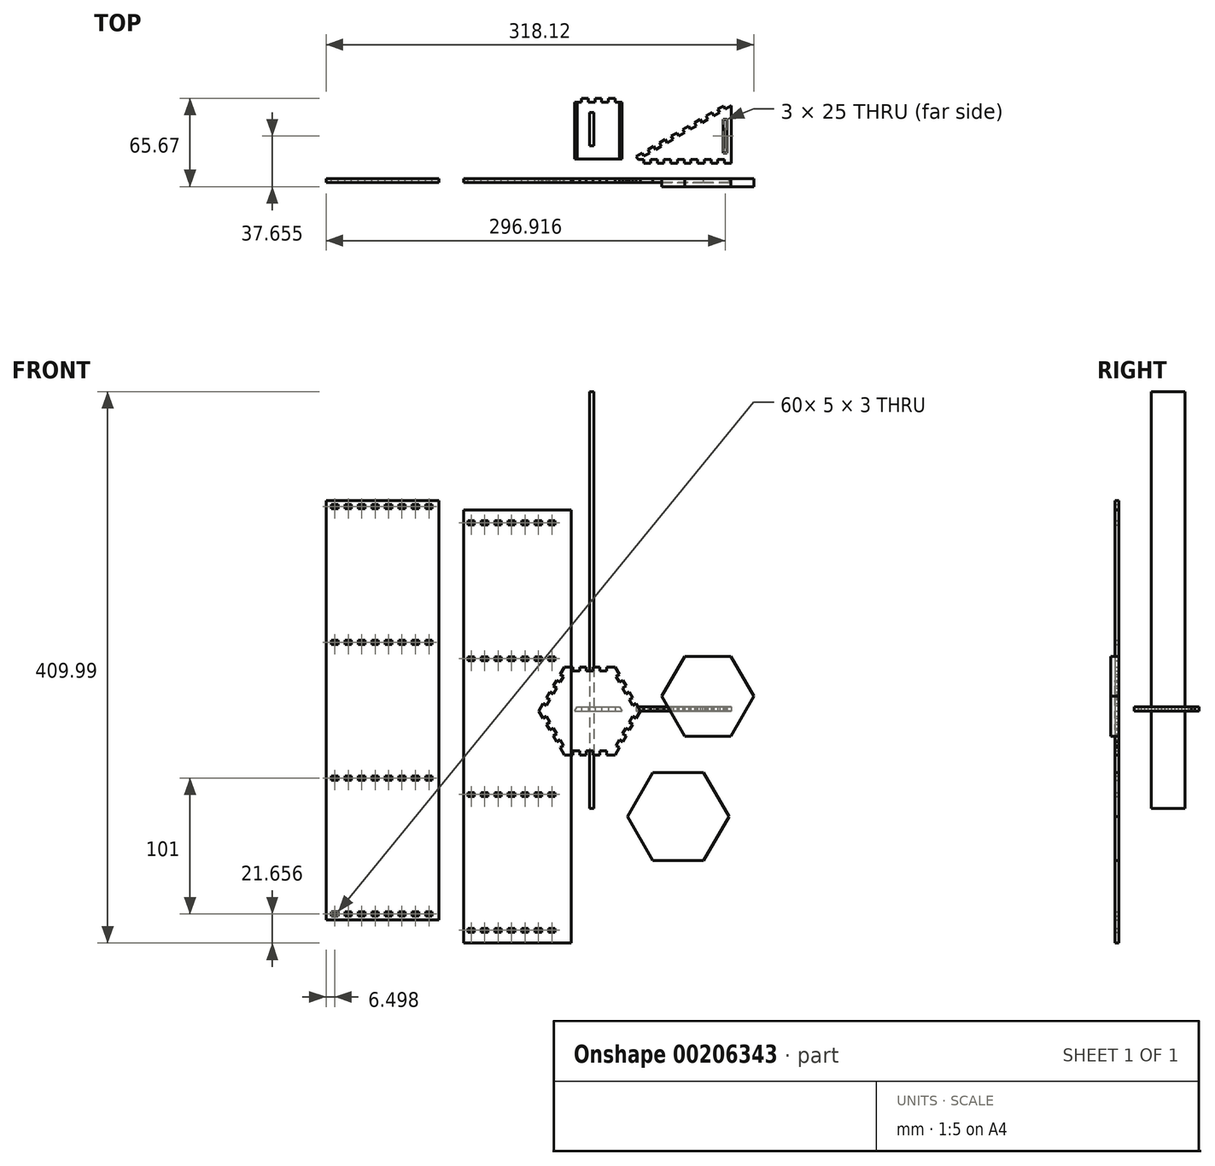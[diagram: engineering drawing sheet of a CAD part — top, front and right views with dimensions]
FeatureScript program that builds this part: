
annotation { "Feature Type Name" : "Feature", "Feature Type Description" : "" }
export const myFeature = defineFeature(function(context is Context, id is Id, definition is map)
    precondition{}
    {
        {
            var Q0;
            Q0=qCreatedBy(makeId("Top.planeOp"),FACE);
            var sketch = newSketch(context, id + "F0", { "sketchPlane" : qUnion([Q0])});
            skLineSegment(sketch, "E0.top", {"start": v(-11.06, 14.67) * mm, "end": v(23.94, 14.67) * mm});
            skLineSegment(sketch, "E0.left", {"start": v(-11.06, 56.67) * mm, "end": v(-11.06, 14.67) * mm});
            skLineSegment(sketch, "E0.right", {"start": v(23.94, 56.67) * mm, "end": v(23.94, 14.67) * mm});
            skLineSegment(sketch, "E1", {"start": v(-6.06, 56.67) * mm, "end": v(-6.06, 59.67) * mm});
            skLineSegment(sketch, "E2", {"start": v(-6.06, 59.67) * mm, "end": v(-1.06, 59.67) * mm});
            skLineSegment(sketch, "E3", {"start": v(-1.06, 59.67) * mm, "end": v(-1.06, 56.67) * mm});
            skLineSegment(sketch, "E4", {"start": v(-11.06, 56.67) * mm, "end": v(-6.06, 56.67) * mm});
            skLineSegment(sketch, "E5", {"start": v(-1.06, 56.67) * mm, "end": v(3.94, 56.67) * mm});
            skLineSegment(sketch, "E6", {"start": v(3.94, 56.67) * mm, "end": v(3.94, 59.67) * mm});
            skLineSegment(sketch, "E7", {"start": v(3.94, 59.67) * mm, "end": v(8.94, 59.67) * mm});
            skLineSegment(sketch, "E8", {"start": v(8.94, 59.67) * mm, "end": v(8.94, 56.67) * mm});
            skLineSegment(sketch, "E9", {"start": v(8.94, 56.67) * mm, "end": v(13.94, 56.67) * mm});
            skLineSegment(sketch, "E10", {"start": v(13.94, 56.67) * mm, "end": v(13.94, 59.67) * mm});
            skLineSegment(sketch, "E11", {"start": v(13.94, 59.67) * mm, "end": v(18.94, 59.67) * mm});
            skLineSegment(sketch, "E12", {"start": v(18.94, 59.67) * mm, "end": v(18.94, 56.67) * mm});
            skLineSegment(sketch, "E13", {"start": v(18.94, 56.67) * mm, "end": v(23.94, 56.67) * mm});
            skSolve(sketch);
        }
        {
            var Q0;
            Q0 = qSketchRegion(id + "F0", true);
            extrude(context, id + "F1", {"entities" : qUnion([Q0]), "depth" : 3 * mm});
        }
        {
            var Q0;
            Q0=makeQuery(id+"F1.opExtrude","CAP_EDGE",EDGE,{"disambiguationData":[OSD([sQuery(id+"F0.wireOp",EDGE,"E0.left")])],"isStart":false});
            var Q1;
            Q1=makeQuery(id+"F1.opExtrude","CAP_EDGE",EDGE,{"disambiguationData":[OSD([sQuery(id+"F0.wireOp",EDGE,"E0.right")])],"isStart":false});
            chamfer(context, id + "F2", {"entities" : qUnion([Q0, Q1]), "chamferType" : ChamferType.OFFSET_ANGLE, "width" : 1.73 * mm, "oppositeDirection" : false, "angle" : 60 * degree, "tangentPropagation" : true});
        }
        {
            var Q0;
            Q0=qCreatedBy(makeId("Front.planeOp"),FACE);
            var sketch = newSketch(context, id + "F3", { "sketchPlane" : qUnion([Q0])});
            skCircle(sketch, "E14.cCircle", {"center": v(0, 0) * mm, "radius": 32.74 * mm, "construction": true});
            skLineSegment(sketch, "E14.0", {"start": v(37.8, 0) * mm, "end": v(34.6, -5.54) * mm});
            skLineSegment(sketch, "E14.1", {"start": v(18.9, -32.74) * mm, "end": v(12.5, -32.74) * mm});
            skLineSegment(sketch, "E14.2", {"start": v(-18.9, -32.74) * mm, "end": v(-22.1, -27.2) * mm});
            skLineSegment(sketch, "E14.3", {"start": v(-37.8, 0) * mm, "end": v(-34.6, 5.54) * mm});
            skLineSegment(sketch, "E14.4", {"start": v(-18.9, 32.74) * mm, "end": v(-12.5, 32.74) * mm});
            skLineSegment(sketch, "E14.5", {"start": v(18.9, 32.74) * mm, "end": v(22.1, 27.2) * mm});
            skPoint(sketch, "E14.0.midPoint", {"position": v(28.35, -16.37) * mm});
            skLineSegment(sketch, "E15", {"start": v(-12.5, 32.74) * mm, "end": v(-12.5, 29.74) * mm});
            skLineSegment(sketch, "E16", {"start": v(-12.5, 29.74) * mm, "end": v(-7.5, 29.74) * mm});
            skLineSegment(sketch, "E17", {"start": v(-7.5, 29.74) * mm, "end": v(-7.5, 32.74) * mm});
            skLineSegment(sketch, "E18", {"start": v(12.5, 32.74) * mm, "end": v(12.5, 29.74) * mm});
            skLineSegment(sketch, "E19", {"start": v(12.5, 29.74) * mm, "end": v(7.5, 29.74) * mm});
            skLineSegment(sketch, "E20", {"start": v(7.5, 29.74) * mm, "end": v(7.5, 32.74) * mm});
            skLineSegment(sketch, "E21", {"start": v(7.5, 32.74) * mm, "end": v(2.5, 32.74) * mm});
            skLineSegment(sketch, "E22", {"start": v(-2.5, 32.74) * mm, "end": v(-2.5, 29.74) * mm});
            skLineSegment(sketch, "E23", {"start": v(-2.5, 29.74) * mm, "end": v(2.5, 29.74) * mm});
            skLineSegment(sketch, "E24", {"start": v(2.5, 29.74) * mm, "end": v(2.5, 32.74) * mm});
            skLineSegment(sketch, "E25.trimOffspring", {"start": v(2.5, 32.74) * mm, "end": v(7.5, 32.74) * mm});
            skLineSegment(sketch, "E26.trimOffspring", {"start": v(-7.5, 32.74) * mm, "end": v(-2.5, 32.74) * mm});
            skLineSegment(sketch, "E27.trimOffspring", {"start": v(12.5, 32.74) * mm, "end": v(18.9, 32.74) * mm});
            skLineSegment(sketch, "E28", {"start": v(-34.6, 5.54) * mm, "end": v(-32, 4.04) * mm});
            skLineSegment(sketch, "E29", {"start": v(-32, 4.04) * mm, "end": v(-29.5, 8.37) * mm});
            skLineSegment(sketch, "E30", {"start": v(-29.5, 8.37) * mm, "end": v(-32.1, 9.87) * mm});
            skLineSegment(sketch, "E31", {"start": v(-29.6, 14.2) * mm, "end": v(-27, 12.7) * mm});
            skLineSegment(sketch, "E32", {"start": v(-27, 12.7) * mm, "end": v(-24.5, 17.03) * mm});
            skLineSegment(sketch, "E33", {"start": v(-24.5, 17.03) * mm, "end": v(-27.1, 18.53) * mm});
            skLineSegment(sketch, "E34", {"start": v(-24.6, 22.86) * mm, "end": v(-22, 21.36) * mm});
            skLineSegment(sketch, "E35", {"start": v(-22, 21.36) * mm, "end": v(-19.5, 25.7) * mm});
            skLineSegment(sketch, "E36", {"start": v(-19.5, 25.7) * mm, "end": v(-22.1, 27.2) * mm});
            skLineSegment(sketch, "E37.trimOffspring", {"start": v(-22.1, 27.2) * mm, "end": v(-18.9, 32.74) * mm});
            skLineSegment(sketch, "E38.trimOffspring", {"start": v(-27.1, 18.53) * mm, "end": v(-24.6, 22.86) * mm});
            skLineSegment(sketch, "E39.trimOffspring", {"start": v(-32.1, 9.87) * mm, "end": v(-29.6, 14.2) * mm});
            skLineSegment(sketch, "E40", {"start": v(22.1, 27.2) * mm, "end": v(19.5, 25.7) * mm});
            skLineSegment(sketch, "E41", {"start": v(19.5, 25.7) * mm, "end": v(22, 21.36) * mm});
            skLineSegment(sketch, "E42", {"start": v(22, 21.36) * mm, "end": v(24.6, 22.86) * mm});
            skLineSegment(sketch, "E43", {"start": v(24.6, 22.86) * mm, "end": v(27.1, 18.53) * mm});
            skLineSegment(sketch, "E44", {"start": v(34.6, 5.54) * mm, "end": v(32, 4.04) * mm});
            skLineSegment(sketch, "E45", {"start": v(32, 4.04) * mm, "end": v(29.5, 8.37) * mm});
            skLineSegment(sketch, "E46", {"start": v(29.5, 8.37) * mm, "end": v(32.1, 9.87) * mm});
            skLineSegment(sketch, "E47", {"start": v(29.6, 14.2) * mm, "end": v(27, 12.7) * mm});
            skLineSegment(sketch, "E48", {"start": v(27, 12.7) * mm, "end": v(24.5, 17.03) * mm});
            skLineSegment(sketch, "E49", {"start": v(24.5, 17.03) * mm, "end": v(27.1, 18.53) * mm});
            skLineSegment(sketch, "E50.trimOffspring", {"start": v(29.6, 14.2) * mm, "end": v(32.1, 9.87) * mm});
            skLineSegment(sketch, "E51.trimOffspring", {"start": v(34.6, 5.54) * mm, "end": v(37.8, 0) * mm});
            skLineSegment(sketch, "E52.1.0", {"start": v(-27, -12.7) * mm, "end": v(-24.5, -17.03) * mm});
            skLineSegment(sketch, "E52.1.1", {"start": v(7.5, -32.74) * mm, "end": v(2.5, -32.74) * mm});
            skLineSegment(sketch, "E52.1.2", {"start": v(-12.5, -29.74) * mm, "end": v(-7.5, -29.74) * mm});
            skLineSegment(sketch, "E52.1.3", {"start": v(-7.5, -32.74) * mm, "end": v(-2.5, -32.74) * mm});
            skLineSegment(sketch, "E52.1.5", {"start": v(-19.5, -25.7) * mm, "end": v(-22, -21.36) * mm});
            skLineSegment(sketch, "E52.1.7", {"start": v(22.1, -27.2) * mm, "end": v(18.9, -32.74) * mm});
            skLineSegment(sketch, "E52.1.8", {"start": v(22, -21.36) * mm, "end": v(19.5, -25.7) * mm});
            skLineSegment(sketch, "E52.1.9", {"start": v(-34.6, -5.54) * mm, "end": v(-37.8, 0) * mm});
            skLineSegment(sketch, "E52.1.10", {"start": v(32, -4.04) * mm, "end": v(29.5, -8.37) * mm});
            skLineSegment(sketch, "E52.1.11", {"start": v(27, -12.7) * mm, "end": v(24.5, -17.03) * mm});
            skLineSegment(sketch, "E52.1.12", {"start": v(-24.6, -22.86) * mm, "end": v(-27.1, -18.53) * mm});
            skLineSegment(sketch, "E52.1.13", {"start": v(2.5, -29.74) * mm, "end": v(-2.5, -29.74) * mm});
            skLineSegment(sketch, "E52.1.14", {"start": v(-12.5, -32.74) * mm, "end": v(-18.9, -32.74) * mm});
            skLineSegment(sketch, "E52.1.15", {"start": v(32.1, -9.87) * mm, "end": v(29.6, -14.2) * mm});
            skLineSegment(sketch, "E52.1.16", {"start": v(12.5, -29.74) * mm, "end": v(7.5, -29.74) * mm});
            skLineSegment(sketch, "E52.1.18", {"start": v(-32, -4.04) * mm, "end": v(-29.5, -8.37) * mm});
            skLineSegment(sketch, "E52.1.19", {"start": v(-29.6, -14.2) * mm, "end": v(-32.1, -9.87) * mm});
            skLineSegment(sketch, "E52.1.20", {"start": v(-2.5, -32.74) * mm, "end": v(-7.5, -32.74) * mm});
            skLineSegment(sketch, "E52.1.21", {"start": v(27.1, -18.53) * mm, "end": v(24.6, -22.86) * mm});
            skLineSegment(sketch, "E52.1.22", {"start": v(-34.6, -5.54) * mm, "end": v(-32, -4.04) * mm});
            skLineSegment(sketch, "E52.1.23", {"start": v(-7.5, -29.74) * mm, "end": v(-7.5, -32.74) * mm});
            skLineSegment(sketch, "E52.1.24", {"start": v(24.6, -22.86) * mm, "end": v(22, -21.36) * mm});
            skLineSegment(sketch, "E52.1.25", {"start": v(-29.5, -8.37) * mm, "end": v(-32.1, -9.87) * mm});
            skLineSegment(sketch, "E52.1.26", {"start": v(24.5, -17.03) * mm, "end": v(27.1, -18.53) * mm});
            skLineSegment(sketch, "E52.1.27", {"start": v(29.5, -8.37) * mm, "end": v(32.1, -9.87) * mm});
            skLineSegment(sketch, "E52.1.28", {"start": v(2.5, -32.74) * mm, "end": v(2.5, -29.74) * mm});
            skLineSegment(sketch, "E52.1.29", {"start": v(-24.5, -17.03) * mm, "end": v(-27.1, -18.53) * mm});
            skLineSegment(sketch, "E52.1.30", {"start": v(-22, -21.36) * mm, "end": v(-24.6, -22.86) * mm});
            skLineSegment(sketch, "E52.1.31", {"start": v(-24.6, -22.86) * mm, "end": v(-27.1, -18.53) * mm});
            skLineSegment(sketch, "E52.1.32", {"start": v(7.5, -29.74) * mm, "end": v(7.5, -32.74) * mm});
            skLineSegment(sketch, "E52.1.33", {"start": v(-29.6, -14.2) * mm, "end": v(-32.1, -9.87) * mm});
            skLineSegment(sketch, "E52.1.34", {"start": v(-12.5, -32.74) * mm, "end": v(-12.5, -29.74) * mm});
            skLineSegment(sketch, "E52.1.35", {"start": v(12.5, -32.74) * mm, "end": v(12.5, -29.74) * mm});
            skLineSegment(sketch, "E52.1.36", {"start": v(-22.1, -27.2) * mm, "end": v(-19.5, -25.7) * mm});
            skLineSegment(sketch, "E52.1.37", {"start": v(-29.6, -14.2) * mm, "end": v(-27, -12.7) * mm});
            skLineSegment(sketch, "E52.1.38", {"start": v(29.6, -14.2) * mm, "end": v(27, -12.7) * mm});
            skLineSegment(sketch, "E52.1.39", {"start": v(19.5, -25.7) * mm, "end": v(22.1, -27.2) * mm});
            skLineSegment(sketch, "E52.1.40", {"start": v(-2.5, -29.74) * mm, "end": v(-2.5, -32.74) * mm});
            skLineSegment(sketch, "E52.1.41", {"start": v(34.6, -5.54) * mm, "end": v(32, -4.04) * mm});
            skSolve(sketch);
        }
        {
            var Q0;
            Q0 = qSketchRegion(id + "F3", true);
            extrude(context, id + "F4", {"entities" : qUnion([Q0]), "depth" : 3 * mm});
        }
        {
            var Q0;
            Q0=qCreatedBy(makeId("Front.planeOp"),FACE);
            var sketch = newSketch(context, id + "F5", { "sketchPlane" : qUnion([Q0])});
            skCircle(sketch, "E53.cCircle", {"center": v(87.8, 10.94) * mm, "radius": 32.74 * mm, "construction": true});
            skLineSegment(sketch, "E53.0", {"start": v(68.9, -21.8) * mm, "end": v(50, 10.94) * mm, "construction": true});
            skLineSegment(sketch, "E53.1", {"start": v(50, 10.94) * mm, "end": v(68.9, 43.68) * mm, "construction": true});
            skLineSegment(sketch, "E53.2", {"start": v(68.9, 43.68) * mm, "end": v(106.7, 43.68) * mm, "construction": true});
            skLineSegment(sketch, "E53.3", {"start": v(106.7, 43.68) * mm, "end": v(125.6, 10.94) * mm, "construction": true});
            skLineSegment(sketch, "E53.4", {"start": v(125.6, 10.94) * mm, "end": v(106.7, -21.8) * mm, "construction": true});
            skLineSegment(sketch, "E53.5", {"start": v(106.7, -21.8) * mm, "end": v(68.9, -21.8) * mm, "construction": true});
            skPoint(sketch, "E53.0.midPoint", {"position": v(59.45, -5.42) * mm});
            skCircle(sketch, "E54.cCircle", {"center": v(87.8, 10.94) * mm, "radius": 29.64 * mm, "construction": true});
            skLineSegment(sketch, "E54.0", {"start": v(122.02, 10.94) * mm, "end": v(104.9, -18.7) * mm});
            skLineSegment(sketch, "E54.1", {"start": v(104.9, -18.7) * mm, "end": v(70.69, -18.7) * mm});
            skLineSegment(sketch, "E54.2", {"start": v(70.69, -18.7) * mm, "end": v(53.58, 10.94) * mm});
            skLineSegment(sketch, "E54.3", {"start": v(53.58, 10.94) * mm, "end": v(70.69, 40.58) * mm});
            skLineSegment(sketch, "E54.4", {"start": v(70.69, 40.58) * mm, "end": v(104.9, 40.58) * mm});
            skLineSegment(sketch, "E54.5", {"start": v(104.9, 40.58) * mm, "end": v(122.02, 10.94) * mm});
            skPoint(sketch, "E54.0.midPoint", {"position": v(113.46, -3.87) * mm});
            skSolve(sketch);
        }
        {
            var Q0;
            Q0 = qSketchRegion(id + "F5", true);
            extrude(context, id + "F6", {"entities" : qUnion([Q0]), "depth" : 6 * mm});
        }
        {
            var Q0;
            Q0=qCreatedBy(makeId("Front.planeOp"),FACE);
            var sketch = newSketch(context, id + "F7", { "sketchPlane" : qUnion([Q0])});
            skCircle(sketch, "E55.cCircle", {"center": v(65.86, -78.59) * mm, "radius": 32.74 * mm, "construction": true});
            skLineSegment(sketch, "E55.0", {"start": v(46.93, -111.3) * mm, "end": v(28.06, -78.56) * mm});
            skLineSegment(sketch, "E55.1", {"start": v(28.06, -78.56) * mm, "end": v(46.98, -45.84) * mm});
            skLineSegment(sketch, "E55.2", {"start": v(46.98, -45.84) * mm, "end": v(84.78, -45.86) * mm});
            skLineSegment(sketch, "E55.3", {"start": v(84.78, -45.86) * mm, "end": v(103.66, -78.61) * mm});
            skLineSegment(sketch, "E55.4", {"start": v(103.66, -78.61) * mm, "end": v(84.73, -111.34) * mm});
            skLineSegment(sketch, "E55.5", {"start": v(84.73, -111.34) * mm, "end": v(46.93, -111.3) * mm});
            skPoint(sketch, "E55.0.midPoint", {"position": v(37.5, -94.93) * mm});
            skSolve(sketch);
        }
        {
            var Q0;
            Q0 = qSketchRegion(id + "F7", true);
            extrude(context, id + "F8", {"entities" : qUnion([Q0]), "depth" : 3 * mm});
        }
        {
            var Q0;
            Q0=qCreatedBy(makeId("Top.planeOp"),FACE);
            var sketch = newSketch(context, id + "F9", { "sketchPlane" : qUnion([Q0])});
            skLineSegment(sketch, "E56", {"start": v(36.03, 14.15) * mm, "end": v(34.63, 16.58) * mm});
            skLineSegment(sketch, "E57", {"start": v(34.63, 16.58) * mm, "end": v(38.96, 19.08) * mm});
            skLineSegment(sketch, "E58", {"start": v(38.96, 19.08) * mm, "end": v(40.36, 16.65) * mm});
            skLineSegment(sketch, "E59", {"start": v(105.32, 14.15) * mm, "end": v(105.32, 11.35) * mm});
            skLineSegment(sketch, "E60", {"start": v(105.32, 11.35) * mm, "end": v(100.32, 11.35) * mm});
            skLineSegment(sketch, "E61", {"start": v(100.32, 11.35) * mm, "end": v(100.32, 14.15) * mm});
            skLineSegment(sketch, "E62", {"start": v(100.32, 14.15) * mm, "end": v(95.32, 14.15) * mm});
            skLineSegment(sketch, "E63.1.0.0", {"start": v(90.32, 11.35) * mm, "end": v(90.32, 14.15) * mm});
            skLineSegment(sketch, "E63.1.0.1", {"start": v(95.32, 11.35) * mm, "end": v(90.32, 11.35) * mm});
            skLineSegment(sketch, "E63.1.0.2", {"start": v(95.32, 14.15) * mm, "end": v(95.32, 11.35) * mm});
            skLineSegment(sketch, "E63.1.0.3", {"start": v(90.32, 14.15) * mm, "end": v(85.32, 14.15) * mm});
            skLineSegment(sketch, "E63.2.0.0", {"start": v(80.32, 11.35) * mm, "end": v(80.32, 14.15) * mm});
            skLineSegment(sketch, "E63.2.0.1", {"start": v(85.32, 11.35) * mm, "end": v(80.32, 11.35) * mm});
            skLineSegment(sketch, "E63.2.0.2", {"start": v(85.32, 14.15) * mm, "end": v(85.32, 11.35) * mm});
            skLineSegment(sketch, "E63.2.0.3", {"start": v(80.32, 14.15) * mm, "end": v(75.32, 14.15) * mm});
            skLineSegment(sketch, "E63.3.0.0", {"start": v(70.32, 11.35) * mm, "end": v(70.32, 14.15) * mm});
            skLineSegment(sketch, "E63.3.0.1", {"start": v(75.32, 11.35) * mm, "end": v(70.32, 11.35) * mm});
            skLineSegment(sketch, "E63.3.0.2", {"start": v(75.32, 14.15) * mm, "end": v(75.32, 11.35) * mm});
            skLineSegment(sketch, "E63.3.0.3", {"start": v(70.32, 14.15) * mm, "end": v(65.32, 14.15) * mm});
            skLineSegment(sketch, "E63.4.0.0", {"start": v(60.32, 11.35) * mm, "end": v(60.32, 14.15) * mm});
            skLineSegment(sketch, "E63.4.0.1", {"start": v(65.32, 11.35) * mm, "end": v(60.32, 11.35) * mm});
            skLineSegment(sketch, "E63.4.0.2", {"start": v(65.32, 14.15) * mm, "end": v(65.32, 11.35) * mm});
            skLineSegment(sketch, "E63.4.0.3", {"start": v(60.32, 14.15) * mm, "end": v(55.32, 14.15) * mm});
            skLineSegment(sketch, "E63.5.0.0", {"start": v(50.32, 11.35) * mm, "end": v(50.32, 14.15) * mm});
            skLineSegment(sketch, "E63.5.0.1", {"start": v(55.32, 11.35) * mm, "end": v(50.32, 11.35) * mm});
            skLineSegment(sketch, "E63.5.0.2", {"start": v(55.32, 14.15) * mm, "end": v(55.32, 11.35) * mm});
            skLineSegment(sketch, "E63.5.0.3", {"start": v(50.32, 14.15) * mm, "end": v(45.32, 14.15) * mm});
            skLineSegment(sketch, "E63.6.0.0", {"start": v(40.32, 11.35) * mm, "end": v(40.32, 14.15) * mm});
            skLineSegment(sketch, "E63.6.0.1", {"start": v(45.32, 11.35) * mm, "end": v(40.32, 11.35) * mm});
            skLineSegment(sketch, "E63.6.0.2", {"start": v(45.32, 14.15) * mm, "end": v(45.32, 11.35) * mm});
            skLineSegment(sketch, "E63.6.0.3", {"start": v(40.32, 14.15) * mm, "end": v(36.03, 14.15) * mm});
            skLineSegment(sketch, "E63.direction1", {"start": v(95.32, 14.15) * mm, "end": v(85.32, 14.15) * mm, "construction": true});
            skLineSegment(sketch, "E64", {"start": v(40.36, 16.65) * mm, "end": v(44.7, 19.15) * mm});
            skLineSegment(sketch, "E65.1.0.0", {"start": v(49.02, 21.65) * mm, "end": v(53.35, 24.15) * mm});
            skLineSegment(sketch, "E65.1.0.1", {"start": v(43.3, 21.58) * mm, "end": v(47.62, 24.08) * mm});
            skLineSegment(sketch, "E65.1.0.2", {"start": v(47.62, 24.08) * mm, "end": v(49.02, 21.65) * mm});
            skLineSegment(sketch, "E65.1.0.3", {"start": v(44.7, 19.15) * mm, "end": v(43.3, 21.58) * mm});
            skLineSegment(sketch, "E65.2.0.0", {"start": v(57.68, 26.65) * mm, "end": v(62.01, 29.15) * mm});
            skLineSegment(sketch, "E65.2.0.1", {"start": v(51.95, 26.58) * mm, "end": v(56.28, 29.08) * mm});
            skLineSegment(sketch, "E65.2.0.2", {"start": v(56.28, 29.08) * mm, "end": v(57.68, 26.65) * mm});
            skLineSegment(sketch, "E65.2.0.3", {"start": v(53.35, 24.15) * mm, "end": v(51.95, 26.58) * mm});
            skLineSegment(sketch, "E65.3.0.0", {"start": v(66.34, 31.65) * mm, "end": v(70.68, 34.15) * mm});
            skLineSegment(sketch, "E65.3.0.1", {"start": v(60.61, 31.58) * mm, "end": v(64.94, 34.08) * mm});
            skLineSegment(sketch, "E65.3.0.2", {"start": v(64.94, 34.08) * mm, "end": v(66.34, 31.65) * mm});
            skLineSegment(sketch, "E65.3.0.3", {"start": v(62.01, 29.15) * mm, "end": v(60.61, 31.58) * mm});
            skLineSegment(sketch, "E65.4.0.0", {"start": v(75, 36.65) * mm, "end": v(79.34, 39.15) * mm});
            skLineSegment(sketch, "E65.4.0.1", {"start": v(69.28, 36.58) * mm, "end": v(73.6, 39.08) * mm});
            skLineSegment(sketch, "E65.4.0.2", {"start": v(73.6, 39.08) * mm, "end": v(75, 36.65) * mm});
            skLineSegment(sketch, "E65.4.0.3", {"start": v(70.68, 34.15) * mm, "end": v(69.28, 36.58) * mm});
            skLineSegment(sketch, "E65.5.0.0", {"start": v(83.67, 41.65) * mm, "end": v(88, 44.15) * mm});
            skLineSegment(sketch, "E65.5.0.1", {"start": v(77.94, 41.58) * mm, "end": v(82.27, 44.08) * mm});
            skLineSegment(sketch, "E65.5.0.2", {"start": v(82.27, 44.08) * mm, "end": v(83.67, 41.65) * mm});
            skLineSegment(sketch, "E65.5.0.3", {"start": v(79.34, 39.15) * mm, "end": v(77.94, 41.58) * mm});
            skLineSegment(sketch, "E65.6.0.0", {"start": v(92.33, 46.65) * mm, "end": v(96.66, 49.15) * mm});
            skLineSegment(sketch, "E65.6.0.1", {"start": v(86.6, 46.58) * mm, "end": v(90.93, 49.08) * mm});
            skLineSegment(sketch, "E65.6.0.2", {"start": v(90.93, 49.08) * mm, "end": v(92.33, 46.65) * mm});
            skLineSegment(sketch, "E65.6.0.3", {"start": v(88, 44.15) * mm, "end": v(86.6, 46.58) * mm});
            skLineSegment(sketch, "E65.7.0.0", {"start": v(100.99, 51.65) * mm, "end": v(105.32, 54.15) * mm});
            skLineSegment(sketch, "E65.7.0.1", {"start": v(95.26, 51.58) * mm, "end": v(99.59, 54.08) * mm});
            skLineSegment(sketch, "E65.7.0.2", {"start": v(99.59, 54.08) * mm, "end": v(100.99, 51.65) * mm});
            skLineSegment(sketch, "E65.7.0.3", {"start": v(96.66, 49.15) * mm, "end": v(95.26, 51.58) * mm});
            skLineSegment(sketch, "E65.direction1", {"start": v(36.03, 14.15) * mm, "end": v(44.7, 19.15) * mm, "construction": true});
            skLineSegment(sketch, "E66", {"start": v(105.32, 54.15) * mm, "end": v(105.32, 14.15) * mm});
            skLineSegment(sketch, "E67.bottom", {"start": v(99.32, 44.15) * mm, "end": v(102.32, 44.15) * mm});
            skLineSegment(sketch, "E67.top", {"start": v(99.32, 19.15) * mm, "end": v(102.32, 19.15) * mm});
            skLineSegment(sketch, "E67.left", {"start": v(99.32, 44.15) * mm, "end": v(99.32, 19.15) * mm});
            skLineSegment(sketch, "E67.right", {"start": v(102.32, 44.15) * mm, "end": v(102.32, 19.15) * mm});
            skSolve(sketch);
        }
        {
            var Q0;
            Q0 = qSketchRegion(id + "F9", true);
            extrude(context, id + "F10", {"entities" : qUnion([Q0]), "depth" : 3 * mm});
        }
        {
            var Q0;
            Q0=qCreatedBy(makeId("Right.planeOp"),FACE);
            var sketch = newSketch(context, id + "F11", { "sketchPlane" : qUnion([Q0])});
            skLineSegment(sketch, "E68.bottom", {"start": v(49.25, 237.39) * mm, "end": v(24.25, 237.39) * mm});
            skLineSegment(sketch, "E68.top", {"start": v(49.25, -72.61) * mm, "end": v(24.25, -72.61) * mm});
            skLineSegment(sketch, "E68.left", {"start": v(49.25, 237.39) * mm, "end": v(49.25, -72.61) * mm});
            skLineSegment(sketch, "E68.right", {"start": v(24.25, 237.39) * mm, "end": v(24.25, -72.61) * mm});
            skSolve(sketch);
        }
        {
            var Q0;
            Q0 = qSketchRegion(id + "F11", true);
            extrude(context, id + "F12", {"entities" : qUnion([Q0]), "depth" : 3 * mm});
        }
        {
            var Q0;
            Q0=qCreatedBy(makeId("Front.planeOp"),FACE);
            var sketch = newSketch(context, id + "F13", { "sketchPlane" : qUnion([Q0])});
            skLineSegment(sketch, "E69.bottom", {"start": v(-93.66, 149.4) * mm, "end": v(-13.66, 149.4) * mm});
            skLineSegment(sketch, "E69.top", {"start": v(-93.66, -172.6) * mm, "end": v(-13.66, -172.6) * mm});
            skLineSegment(sketch, "E69.left", {"start": v(-93.66, 149.4) * mm, "end": v(-93.66, -172.6) * mm});
            skLineSegment(sketch, "E69.right", {"start": v(-13.66, 149.4) * mm, "end": v(-13.66, -172.6) * mm});
            skLineSegment(sketch, "E70.bottom", {"start": v(-90.66, -161.6) * mm, "end": v(-85.66, -161.6) * mm});
            skLineSegment(sketch, "E70.top", {"start": v(-90.66, -164.6) * mm, "end": v(-85.66, -164.6) * mm});
            skLineSegment(sketch, "E70.left", {"start": v(-90.66, -161.6) * mm, "end": v(-90.66, -164.6) * mm});
            skLineSegment(sketch, "E70.right", {"start": v(-85.66, -161.6) * mm, "end": v(-85.66, -164.6) * mm});
            skLineSegment(sketch, "E71.1.0.0", {"start": v(-80.66, -161.6) * mm, "end": v(-75.66, -161.6) * mm});
            skLineSegment(sketch, "E71.1.0.1", {"start": v(-80.66, -164.6) * mm, "end": v(-75.66, -164.6) * mm});
            skLineSegment(sketch, "E71.1.0.2", {"start": v(-80.66, -161.6) * mm, "end": v(-80.66, -164.6) * mm});
            skLineSegment(sketch, "E71.1.0.3", {"start": v(-75.66, -161.6) * mm, "end": v(-75.66, -164.6) * mm});
            skLineSegment(sketch, "E71.2.0.0", {"start": v(-70.66, -161.6) * mm, "end": v(-65.66, -161.6) * mm});
            skLineSegment(sketch, "E71.2.0.1", {"start": v(-70.66, -164.6) * mm, "end": v(-65.66, -164.6) * mm});
            skLineSegment(sketch, "E71.2.0.2", {"start": v(-70.66, -161.6) * mm, "end": v(-70.66, -164.6) * mm});
            skLineSegment(sketch, "E71.2.0.3", {"start": v(-65.66, -161.6) * mm, "end": v(-65.66, -164.6) * mm});
            skLineSegment(sketch, "E71.3.0.0", {"start": v(-60.66, -161.6) * mm, "end": v(-55.66, -161.6) * mm});
            skLineSegment(sketch, "E71.3.0.1", {"start": v(-60.66, -164.6) * mm, "end": v(-55.66, -164.6) * mm});
            skLineSegment(sketch, "E71.3.0.2", {"start": v(-60.66, -161.6) * mm, "end": v(-60.66, -164.6) * mm});
            skLineSegment(sketch, "E71.3.0.3", {"start": v(-55.66, -161.6) * mm, "end": v(-55.66, -164.6) * mm});
            skLineSegment(sketch, "E71.4.0.0", {"start": v(-50.66, -161.6) * mm, "end": v(-45.66, -161.6) * mm});
            skLineSegment(sketch, "E71.4.0.1", {"start": v(-50.66, -164.6) * mm, "end": v(-45.66, -164.6) * mm});
            skLineSegment(sketch, "E71.4.0.2", {"start": v(-50.66, -161.6) * mm, "end": v(-50.66, -164.6) * mm});
            skLineSegment(sketch, "E71.4.0.3", {"start": v(-45.66, -161.6) * mm, "end": v(-45.66, -164.6) * mm});
            skLineSegment(sketch, "E71.5.0.0", {"start": v(-40.66, -161.6) * mm, "end": v(-35.66, -161.6) * mm});
            skLineSegment(sketch, "E71.5.0.1", {"start": v(-40.66, -164.6) * mm, "end": v(-35.66, -164.6) * mm});
            skLineSegment(sketch, "E71.5.0.2", {"start": v(-40.66, -161.6) * mm, "end": v(-40.66, -164.6) * mm});
            skLineSegment(sketch, "E71.5.0.3", {"start": v(-35.66, -161.6) * mm, "end": v(-35.66, -164.6) * mm});
            skLineSegment(sketch, "E71.6.0.0", {"start": v(-30.66, -161.6) * mm, "end": v(-25.66, -161.6) * mm});
            skLineSegment(sketch, "E71.6.0.1", {"start": v(-30.66, -164.6) * mm, "end": v(-25.66, -164.6) * mm});
            skLineSegment(sketch, "E71.6.0.2", {"start": v(-30.66, -161.6) * mm, "end": v(-30.66, -164.6) * mm});
            skLineSegment(sketch, "E71.6.0.3", {"start": v(-25.66, -161.6) * mm, "end": v(-25.66, -164.6) * mm});
            skLineSegment(sketch, "E71.direction1", {"start": v(-90.66, -164.6) * mm, "end": v(-80.66, -164.6) * mm, "construction": true});
            skLineSegment(sketch, "E72.0.1.0", {"start": v(-60.66, -60.6) * mm, "end": v(-55.66, -60.6) * mm});
            skLineSegment(sketch, "E72.0.1.1", {"start": v(-40.66, -63.6) * mm, "end": v(-35.66, -63.6) * mm});
            skLineSegment(sketch, "E72.0.1.2", {"start": v(-90.66, -63.6) * mm, "end": v(-80.66, -63.6) * mm, "construction": true});
            skLineSegment(sketch, "E72.0.1.3", {"start": v(-90.66, -60.6) * mm, "end": v(-85.66, -60.6) * mm});
            skLineSegment(sketch, "E72.0.1.4", {"start": v(-50.66, -63.6) * mm, "end": v(-45.66, -63.6) * mm});
            skLineSegment(sketch, "E72.0.1.5", {"start": v(-30.66, -63.6) * mm, "end": v(-25.66, -63.6) * mm});
            skLineSegment(sketch, "E72.0.1.6", {"start": v(-50.66, -60.6) * mm, "end": v(-45.66, -60.6) * mm});
            skLineSegment(sketch, "E72.0.1.7", {"start": v(-80.66, -60.6) * mm, "end": v(-75.66, -60.6) * mm});
            skLineSegment(sketch, "E72.0.1.8", {"start": v(-80.66, -63.6) * mm, "end": v(-75.66, -63.6) * mm});
            skLineSegment(sketch, "E72.0.1.9", {"start": v(-70.66, -60.6) * mm, "end": v(-65.66, -60.6) * mm});
            skLineSegment(sketch, "E72.0.1.10", {"start": v(-70.66, -63.6) * mm, "end": v(-65.66, -63.6) * mm});
            skLineSegment(sketch, "E72.0.1.11", {"start": v(-30.66, -60.6) * mm, "end": v(-25.66, -60.6) * mm});
            skLineSegment(sketch, "E72.0.1.12", {"start": v(-40.66, -60.6) * mm, "end": v(-35.66, -60.6) * mm});
            skLineSegment(sketch, "E72.0.1.13", {"start": v(-60.66, -63.6) * mm, "end": v(-55.66, -63.6) * mm});
            skLineSegment(sketch, "E72.0.1.14", {"start": v(-90.66, -63.6) * mm, "end": v(-85.66, -63.6) * mm});
            skLineSegment(sketch, "E72.0.1.15", {"start": v(-90.66, -60.6) * mm, "end": v(-90.66, -63.6) * mm});
            skLineSegment(sketch, "E72.0.1.16", {"start": v(-80.66, -60.6) * mm, "end": v(-80.66, -63.6) * mm});
            skLineSegment(sketch, "E72.0.1.17", {"start": v(-40.66, -60.6) * mm, "end": v(-40.66, -63.6) * mm});
            skLineSegment(sketch, "E72.0.1.18", {"start": v(-45.66, -60.6) * mm, "end": v(-45.66, -63.6) * mm});
            skLineSegment(sketch, "E72.0.1.19", {"start": v(-65.66, -60.6) * mm, "end": v(-65.66, -63.6) * mm});
            skLineSegment(sketch, "E72.0.1.20", {"start": v(-75.66, -60.6) * mm, "end": v(-75.66, -63.6) * mm});
            skLineSegment(sketch, "E72.0.1.21", {"start": v(-35.66, -60.6) * mm, "end": v(-35.66, -63.6) * mm});
            skLineSegment(sketch, "E72.0.1.22", {"start": v(-25.66, -60.6) * mm, "end": v(-25.66, -63.6) * mm});
            skLineSegment(sketch, "E72.0.1.23", {"start": v(-85.66, -60.6) * mm, "end": v(-85.66, -63.6) * mm});
            skLineSegment(sketch, "E72.0.1.24", {"start": v(-50.66, -60.6) * mm, "end": v(-50.66, -63.6) * mm});
            skLineSegment(sketch, "E72.0.1.25", {"start": v(-70.66, -60.6) * mm, "end": v(-70.66, -63.6) * mm});
            skLineSegment(sketch, "E72.0.1.26", {"start": v(-30.66, -60.6) * mm, "end": v(-30.66, -63.6) * mm});
            skLineSegment(sketch, "E72.0.1.27", {"start": v(-60.66, -60.6) * mm, "end": v(-60.66, -63.6) * mm});
            skLineSegment(sketch, "E72.0.1.28", {"start": v(-55.66, -60.6) * mm, "end": v(-55.66, -63.6) * mm});
            skLineSegment(sketch, "E72.0.2.0", {"start": v(-60.66, 40.4) * mm, "end": v(-55.66, 40.4) * mm});
            skLineSegment(sketch, "E72.0.2.1", {"start": v(-40.66, 37.4) * mm, "end": v(-35.66, 37.4) * mm});
            skLineSegment(sketch, "E72.0.2.2", {"start": v(-90.66, 37.4) * mm, "end": v(-80.66, 37.4) * mm, "construction": true});
            skLineSegment(sketch, "E72.0.2.3", {"start": v(-90.66, 40.4) * mm, "end": v(-85.66, 40.4) * mm});
            skLineSegment(sketch, "E72.0.2.4", {"start": v(-50.66, 37.4) * mm, "end": v(-45.66, 37.4) * mm});
            skLineSegment(sketch, "E72.0.2.5", {"start": v(-30.66, 37.4) * mm, "end": v(-25.66, 37.4) * mm});
            skLineSegment(sketch, "E72.0.2.6", {"start": v(-50.66, 40.4) * mm, "end": v(-45.66, 40.4) * mm});
            skLineSegment(sketch, "E72.0.2.7", {"start": v(-80.66, 40.4) * mm, "end": v(-75.66, 40.4) * mm});
            skLineSegment(sketch, "E72.0.2.8", {"start": v(-80.66, 37.4) * mm, "end": v(-75.66, 37.4) * mm});
            skLineSegment(sketch, "E72.0.2.9", {"start": v(-70.66, 40.4) * mm, "end": v(-65.66, 40.4) * mm});
            skLineSegment(sketch, "E72.0.2.10", {"start": v(-70.66, 37.4) * mm, "end": v(-65.66, 37.4) * mm});
            skLineSegment(sketch, "E72.0.2.11", {"start": v(-30.66, 40.4) * mm, "end": v(-25.66, 40.4) * mm});
            skLineSegment(sketch, "E72.0.2.12", {"start": v(-40.66, 40.4) * mm, "end": v(-35.66, 40.4) * mm});
            skLineSegment(sketch, "E72.0.2.13", {"start": v(-60.66, 37.4) * mm, "end": v(-55.66, 37.4) * mm});
            skLineSegment(sketch, "E72.0.2.14", {"start": v(-90.66, 37.4) * mm, "end": v(-85.66, 37.4) * mm});
            skLineSegment(sketch, "E72.0.2.15", {"start": v(-90.66, 40.4) * mm, "end": v(-90.66, 37.4) * mm});
            skLineSegment(sketch, "E72.0.2.16", {"start": v(-80.66, 40.4) * mm, "end": v(-80.66, 37.4) * mm});
            skLineSegment(sketch, "E72.0.2.17", {"start": v(-40.66, 40.4) * mm, "end": v(-40.66, 37.4) * mm});
            skLineSegment(sketch, "E72.0.2.18", {"start": v(-45.66, 40.4) * mm, "end": v(-45.66, 37.4) * mm});
            skLineSegment(sketch, "E72.0.2.19", {"start": v(-65.66, 40.4) * mm, "end": v(-65.66, 37.4) * mm});
            skLineSegment(sketch, "E72.0.2.20", {"start": v(-75.66, 40.4) * mm, "end": v(-75.66, 37.4) * mm});
            skLineSegment(sketch, "E72.0.2.21", {"start": v(-35.66, 40.4) * mm, "end": v(-35.66, 37.4) * mm});
            skLineSegment(sketch, "E72.0.2.22", {"start": v(-25.66, 40.4) * mm, "end": v(-25.66, 37.4) * mm});
            skLineSegment(sketch, "E72.0.2.23", {"start": v(-85.66, 40.4) * mm, "end": v(-85.66, 37.4) * mm});
            skLineSegment(sketch, "E72.0.2.24", {"start": v(-50.66, 40.4) * mm, "end": v(-50.66, 37.4) * mm});
            skLineSegment(sketch, "E72.0.2.25", {"start": v(-70.66, 40.4) * mm, "end": v(-70.66, 37.4) * mm});
            skLineSegment(sketch, "E72.0.2.26", {"start": v(-30.66, 40.4) * mm, "end": v(-30.66, 37.4) * mm});
            skLineSegment(sketch, "E72.0.2.27", {"start": v(-60.66, 40.4) * mm, "end": v(-60.66, 37.4) * mm});
            skLineSegment(sketch, "E72.0.2.28", {"start": v(-55.66, 40.4) * mm, "end": v(-55.66, 37.4) * mm});
            skLineSegment(sketch, "E72.0.3.0", {"start": v(-60.66, 141.4) * mm, "end": v(-55.66, 141.4) * mm});
            skLineSegment(sketch, "E72.0.3.1", {"start": v(-40.66, 138.4) * mm, "end": v(-35.66, 138.4) * mm});
            skLineSegment(sketch, "E72.0.3.2", {"start": v(-90.66, 138.4) * mm, "end": v(-80.66, 138.4) * mm, "construction": true});
            skLineSegment(sketch, "E72.0.3.3", {"start": v(-90.66, 141.4) * mm, "end": v(-85.66, 141.4) * mm});
            skLineSegment(sketch, "E72.0.3.4", {"start": v(-50.66, 138.4) * mm, "end": v(-45.66, 138.4) * mm});
            skLineSegment(sketch, "E72.0.3.5", {"start": v(-30.66, 138.4) * mm, "end": v(-25.66, 138.4) * mm});
            skLineSegment(sketch, "E72.0.3.6", {"start": v(-50.66, 141.4) * mm, "end": v(-45.66, 141.4) * mm});
            skLineSegment(sketch, "E72.0.3.7", {"start": v(-80.66, 141.4) * mm, "end": v(-75.66, 141.4) * mm});
            skLineSegment(sketch, "E72.0.3.8", {"start": v(-80.66, 138.4) * mm, "end": v(-75.66, 138.4) * mm});
            skLineSegment(sketch, "E72.0.3.9", {"start": v(-70.66, 141.4) * mm, "end": v(-65.66, 141.4) * mm});
            skLineSegment(sketch, "E72.0.3.10", {"start": v(-70.66, 138.4) * mm, "end": v(-65.66, 138.4) * mm});
            skLineSegment(sketch, "E72.0.3.11", {"start": v(-30.66, 141.4) * mm, "end": v(-25.66, 141.4) * mm});
            skLineSegment(sketch, "E72.0.3.12", {"start": v(-40.66, 141.4) * mm, "end": v(-35.66, 141.4) * mm});
            skLineSegment(sketch, "E72.0.3.13", {"start": v(-60.66, 138.4) * mm, "end": v(-55.66, 138.4) * mm});
            skLineSegment(sketch, "E72.0.3.14", {"start": v(-90.66, 138.4) * mm, "end": v(-85.66, 138.4) * mm});
            skLineSegment(sketch, "E72.0.3.15", {"start": v(-90.66, 141.4) * mm, "end": v(-90.66, 138.4) * mm});
            skLineSegment(sketch, "E72.0.3.16", {"start": v(-80.66, 141.4) * mm, "end": v(-80.66, 138.4) * mm});
            skLineSegment(sketch, "E72.0.3.17", {"start": v(-40.66, 141.4) * mm, "end": v(-40.66, 138.4) * mm});
            skLineSegment(sketch, "E72.0.3.18", {"start": v(-45.66, 141.4) * mm, "end": v(-45.66, 138.4) * mm});
            skLineSegment(sketch, "E72.0.3.19", {"start": v(-65.66, 141.4) * mm, "end": v(-65.66, 138.4) * mm});
            skLineSegment(sketch, "E72.0.3.20", {"start": v(-75.66, 141.4) * mm, "end": v(-75.66, 138.4) * mm});
            skLineSegment(sketch, "E72.0.3.21", {"start": v(-35.66, 141.4) * mm, "end": v(-35.66, 138.4) * mm});
            skLineSegment(sketch, "E72.0.3.22", {"start": v(-25.66, 141.4) * mm, "end": v(-25.66, 138.4) * mm});
            skLineSegment(sketch, "E72.0.3.23", {"start": v(-85.66, 141.4) * mm, "end": v(-85.66, 138.4) * mm});
            skLineSegment(sketch, "E72.0.3.24", {"start": v(-50.66, 141.4) * mm, "end": v(-50.66, 138.4) * mm});
            skLineSegment(sketch, "E72.0.3.25", {"start": v(-70.66, 141.4) * mm, "end": v(-70.66, 138.4) * mm});
            skLineSegment(sketch, "E72.0.3.26", {"start": v(-30.66, 141.4) * mm, "end": v(-30.66, 138.4) * mm});
            skLineSegment(sketch, "E72.0.3.27", {"start": v(-60.66, 141.4) * mm, "end": v(-60.66, 138.4) * mm});
            skLineSegment(sketch, "E72.0.3.28", {"start": v(-55.66, 141.4) * mm, "end": v(-55.66, 138.4) * mm});
            skLineSegment(sketch, "E72.direction1", {"start": v(-90.66, -164.6) * mm, "end": v(-65.66, -164.6) * mm, "construction": true});
            skLineSegment(sketch, "E72.direction2", {"start": v(-90.66, -164.6) * mm, "end": v(-90.66, -63.6) * mm, "construction": true});
            skSolve(sketch);
        }
        {
            var Q0;
            Q0=makeQuery(id+"F13.imprint","IMPRINT",FACE,{"disambiguationData":[TD([[makeQuery(id+"F13.imprint","IMPRINT",EDGE,{"derivedFrom":sQuery(id+"F13.wireOp",EDGE,"E69.bottom")}),-1.0]])]});
            extrude(context, id + "F14", {"entities" : qUnion([Q0]), "depth" : 3 * mm});
        }
        {
            var Q0;
            Q0=qCreatedBy(makeId("Front.planeOp"),FACE);
            var sketch = newSketch(context, id + "F15", { "sketchPlane" : qUnion([Q0])});
            skLineSegment(sketch, "E73.bottom", {"start": v(-196.1, 156.56) * mm, "end": v(-112.1, 156.56) * mm});
            skLineSegment(sketch, "E73.top", {"start": v(-196.1, -155.44) * mm, "end": v(-112.1, -155.44) * mm});
            skLineSegment(sketch, "E73.left", {"start": v(-196.1, 156.56) * mm, "end": v(-196.1, -155.44) * mm});
            skLineSegment(sketch, "E73.right", {"start": v(-112.1, 156.56) * mm, "end": v(-112.1, -155.44) * mm});
            skLineSegment(sketch, "E74.bottom", {"start": v(-192.1, -149.44) * mm, "end": v(-187.1, -149.44) * mm});
            skLineSegment(sketch, "E74.top", {"start": v(-192.1, -152.44) * mm, "end": v(-187.1, -152.44) * mm});
            skLineSegment(sketch, "E74.left", {"start": v(-192.1, -149.44) * mm, "end": v(-192.1, -152.44) * mm});
            skLineSegment(sketch, "E74.right", {"start": v(-187.1, -149.44) * mm, "end": v(-187.1, -152.44) * mm});
            skLineSegment(sketch, "E75.1.0.0", {"start": v(-182.1, -152.44) * mm, "end": v(-177.1, -152.44) * mm});
            skLineSegment(sketch, "E75.1.0.1", {"start": v(-182.1, -149.44) * mm, "end": v(-177.1, -149.44) * mm});
            skLineSegment(sketch, "E75.1.0.2", {"start": v(-177.1, -149.44) * mm, "end": v(-177.1, -152.44) * mm});
            skLineSegment(sketch, "E75.1.0.3", {"start": v(-182.1, -149.44) * mm, "end": v(-182.1, -152.44) * mm});
            skLineSegment(sketch, "E75.2.0.0", {"start": v(-172.1, -152.44) * mm, "end": v(-167.1, -152.44) * mm});
            skLineSegment(sketch, "E75.2.0.1", {"start": v(-172.1, -149.44) * mm, "end": v(-167.1, -149.44) * mm});
            skLineSegment(sketch, "E75.2.0.2", {"start": v(-167.1, -149.44) * mm, "end": v(-167.1, -152.44) * mm});
            skLineSegment(sketch, "E75.2.0.3", {"start": v(-172.1, -149.44) * mm, "end": v(-172.1, -152.44) * mm});
            skLineSegment(sketch, "E75.3.0.0", {"start": v(-162.1, -152.44) * mm, "end": v(-157.1, -152.44) * mm});
            skLineSegment(sketch, "E75.3.0.1", {"start": v(-162.1, -149.44) * mm, "end": v(-157.1, -149.44) * mm});
            skLineSegment(sketch, "E75.3.0.2", {"start": v(-157.1, -149.44) * mm, "end": v(-157.1, -152.44) * mm});
            skLineSegment(sketch, "E75.3.0.3", {"start": v(-162.1, -149.44) * mm, "end": v(-162.1, -152.44) * mm});
            skLineSegment(sketch, "E75.4.0.0", {"start": v(-152.1, -152.44) * mm, "end": v(-147.1, -152.44) * mm});
            skLineSegment(sketch, "E75.4.0.1", {"start": v(-152.1, -149.44) * mm, "end": v(-147.1, -149.44) * mm});
            skLineSegment(sketch, "E75.4.0.2", {"start": v(-147.1, -149.44) * mm, "end": v(-147.1, -152.44) * mm});
            skLineSegment(sketch, "E75.4.0.3", {"start": v(-152.1, -149.44) * mm, "end": v(-152.1, -152.44) * mm});
            skLineSegment(sketch, "E75.5.0.0", {"start": v(-142.1, -152.44) * mm, "end": v(-137.1, -152.44) * mm});
            skLineSegment(sketch, "E75.5.0.1", {"start": v(-142.1, -149.44) * mm, "end": v(-137.1, -149.44) * mm});
            skLineSegment(sketch, "E75.5.0.2", {"start": v(-137.1, -149.44) * mm, "end": v(-137.1, -152.44) * mm});
            skLineSegment(sketch, "E75.5.0.3", {"start": v(-142.1, -149.44) * mm, "end": v(-142.1, -152.44) * mm});
            skLineSegment(sketch, "E75.6.0.0", {"start": v(-132.1, -152.44) * mm, "end": v(-127.1, -152.44) * mm});
            skLineSegment(sketch, "E75.6.0.1", {"start": v(-132.1, -149.44) * mm, "end": v(-127.1, -149.44) * mm});
            skLineSegment(sketch, "E75.6.0.2", {"start": v(-127.1, -149.44) * mm, "end": v(-127.1, -152.44) * mm});
            skLineSegment(sketch, "E75.6.0.3", {"start": v(-132.1, -149.44) * mm, "end": v(-132.1, -152.44) * mm});
            skLineSegment(sketch, "E75.7.0.0", {"start": v(-122.1, -152.44) * mm, "end": v(-117.1, -152.44) * mm});
            skLineSegment(sketch, "E75.7.0.1", {"start": v(-122.1, -149.44) * mm, "end": v(-117.1, -149.44) * mm});
            skLineSegment(sketch, "E75.7.0.2", {"start": v(-117.1, -149.44) * mm, "end": v(-117.1, -152.44) * mm});
            skLineSegment(sketch, "E75.7.0.3", {"start": v(-122.1, -149.44) * mm, "end": v(-122.1, -152.44) * mm});
            skLineSegment(sketch, "E75.direction1", {"start": v(-192.1, -152.44) * mm, "end": v(-182.1, -152.44) * mm, "construction": true});
            skLineSegment(sketch, "E76.0.1.0", {"start": v(-172.1, -51.44) * mm, "end": v(-167.1, -51.44) * mm});
            skLineSegment(sketch, "E76.0.1.1", {"start": v(-182.1, -48.44) * mm, "end": v(-177.1, -48.44) * mm});
            skLineSegment(sketch, "E76.0.1.2", {"start": v(-182.1, -51.44) * mm, "end": v(-177.1, -51.44) * mm});
            skLineSegment(sketch, "E76.0.1.3", {"start": v(-152.1, -48.44) * mm, "end": v(-147.1, -48.44) * mm});
            skLineSegment(sketch, "E76.0.1.4", {"start": v(-162.1, -48.44) * mm, "end": v(-157.1, -48.44) * mm});
            skLineSegment(sketch, "E76.0.1.5", {"start": v(-122.1, -48.44) * mm, "end": v(-117.1, -48.44) * mm});
            skLineSegment(sketch, "E76.0.1.6", {"start": v(-132.1, -51.44) * mm, "end": v(-127.1, -51.44) * mm});
            skLineSegment(sketch, "E76.0.1.7", {"start": v(-142.1, -51.44) * mm, "end": v(-137.1, -51.44) * mm});
            skLineSegment(sketch, "E76.0.1.8", {"start": v(-142.1, -48.44) * mm, "end": v(-137.1, -48.44) * mm});
            skLineSegment(sketch, "E76.0.1.9", {"start": v(-152.1, -51.44) * mm, "end": v(-147.1, -51.44) * mm});
            skLineSegment(sketch, "E76.0.1.10", {"start": v(-132.1, -48.44) * mm, "end": v(-127.1, -48.44) * mm});
            skLineSegment(sketch, "E76.0.1.11", {"start": v(-192.1, -51.44) * mm, "end": v(-182.1, -51.44) * mm, "construction": true});
            skLineSegment(sketch, "E76.0.1.12", {"start": v(-162.1, -51.44) * mm, "end": v(-157.1, -51.44) * mm});
            skLineSegment(sketch, "E76.0.1.13", {"start": v(-172.1, -48.44) * mm, "end": v(-167.1, -48.44) * mm});
            skLineSegment(sketch, "E76.0.1.14", {"start": v(-122.1, -51.44) * mm, "end": v(-117.1, -51.44) * mm});
            skLineSegment(sketch, "E76.0.1.15", {"start": v(-192.1, -48.44) * mm, "end": v(-187.1, -48.44) * mm});
            skLineSegment(sketch, "E76.0.1.16", {"start": v(-192.1, -51.44) * mm, "end": v(-187.1, -51.44) * mm});
            skLineSegment(sketch, "E76.0.1.17", {"start": v(-182.1, -48.44) * mm, "end": v(-182.1, -51.44) * mm});
            skLineSegment(sketch, "E76.0.1.18", {"start": v(-152.1, -48.44) * mm, "end": v(-152.1, -51.44) * mm});
            skLineSegment(sketch, "E76.0.1.19", {"start": v(-142.1, -48.44) * mm, "end": v(-142.1, -51.44) * mm});
            skLineSegment(sketch, "E76.0.1.20", {"start": v(-177.1, -48.44) * mm, "end": v(-177.1, -51.44) * mm});
            skLineSegment(sketch, "E76.0.1.21", {"start": v(-187.1, -48.44) * mm, "end": v(-187.1, -51.44) * mm});
            skLineSegment(sketch, "E76.0.1.22", {"start": v(-192.1, -48.44) * mm, "end": v(-192.1, -51.44) * mm});
            skLineSegment(sketch, "E76.0.1.23", {"start": v(-127.1, -48.44) * mm, "end": v(-127.1, -51.44) * mm});
            skLineSegment(sketch, "E76.0.1.24", {"start": v(-132.1, -48.44) * mm, "end": v(-132.1, -51.44) * mm});
            skLineSegment(sketch, "E76.0.1.25", {"start": v(-157.1, -48.44) * mm, "end": v(-157.1, -51.44) * mm});
            skLineSegment(sketch, "E76.0.1.26", {"start": v(-117.1, -48.44) * mm, "end": v(-117.1, -51.44) * mm});
            skLineSegment(sketch, "E76.0.1.27", {"start": v(-147.1, -48.44) * mm, "end": v(-147.1, -51.44) * mm});
            skLineSegment(sketch, "E76.0.1.28", {"start": v(-162.1, -48.44) * mm, "end": v(-162.1, -51.44) * mm});
            skLineSegment(sketch, "E76.0.1.29", {"start": v(-122.1, -48.44) * mm, "end": v(-122.1, -51.44) * mm});
            skLineSegment(sketch, "E76.0.1.30", {"start": v(-137.1, -48.44) * mm, "end": v(-137.1, -51.44) * mm});
            skLineSegment(sketch, "E76.0.1.31", {"start": v(-167.1, -48.44) * mm, "end": v(-167.1, -51.44) * mm});
            skLineSegment(sketch, "E76.0.1.32", {"start": v(-172.1, -48.44) * mm, "end": v(-172.1, -51.44) * mm});
            skLineSegment(sketch, "E76.0.2.0", {"start": v(-172.1, 49.56) * mm, "end": v(-167.1, 49.56) * mm});
            skLineSegment(sketch, "E76.0.2.1", {"start": v(-182.1, 52.56) * mm, "end": v(-177.1, 52.56) * mm});
            skLineSegment(sketch, "E76.0.2.2", {"start": v(-182.1, 49.56) * mm, "end": v(-177.1, 49.56) * mm});
            skLineSegment(sketch, "E76.0.2.3", {"start": v(-152.1, 52.56) * mm, "end": v(-147.1, 52.56) * mm});
            skLineSegment(sketch, "E76.0.2.4", {"start": v(-162.1, 52.56) * mm, "end": v(-157.1, 52.56) * mm});
            skLineSegment(sketch, "E76.0.2.5", {"start": v(-122.1, 52.56) * mm, "end": v(-117.1, 52.56) * mm});
            skLineSegment(sketch, "E76.0.2.6", {"start": v(-132.1, 49.56) * mm, "end": v(-127.1, 49.56) * mm});
            skLineSegment(sketch, "E76.0.2.7", {"start": v(-142.1, 49.56) * mm, "end": v(-137.1, 49.56) * mm});
            skLineSegment(sketch, "E76.0.2.8", {"start": v(-142.1, 52.56) * mm, "end": v(-137.1, 52.56) * mm});
            skLineSegment(sketch, "E76.0.2.9", {"start": v(-152.1, 49.56) * mm, "end": v(-147.1, 49.56) * mm});
            skLineSegment(sketch, "E76.0.2.10", {"start": v(-132.1, 52.56) * mm, "end": v(-127.1, 52.56) * mm});
            skLineSegment(sketch, "E76.0.2.11", {"start": v(-192.1, 49.56) * mm, "end": v(-182.1, 49.56) * mm, "construction": true});
            skLineSegment(sketch, "E76.0.2.12", {"start": v(-162.1, 49.56) * mm, "end": v(-157.1, 49.56) * mm});
            skLineSegment(sketch, "E76.0.2.13", {"start": v(-172.1, 52.56) * mm, "end": v(-167.1, 52.56) * mm});
            skLineSegment(sketch, "E76.0.2.14", {"start": v(-122.1, 49.56) * mm, "end": v(-117.1, 49.56) * mm});
            skLineSegment(sketch, "E76.0.2.15", {"start": v(-192.1, 52.56) * mm, "end": v(-187.1, 52.56) * mm});
            skLineSegment(sketch, "E76.0.2.16", {"start": v(-192.1, 49.56) * mm, "end": v(-187.1, 49.56) * mm});
            skLineSegment(sketch, "E76.0.2.17", {"start": v(-182.1, 52.56) * mm, "end": v(-182.1, 49.56) * mm});
            skLineSegment(sketch, "E76.0.2.18", {"start": v(-152.1, 52.56) * mm, "end": v(-152.1, 49.56) * mm});
            skLineSegment(sketch, "E76.0.2.19", {"start": v(-142.1, 52.56) * mm, "end": v(-142.1, 49.56) * mm});
            skLineSegment(sketch, "E76.0.2.20", {"start": v(-177.1, 52.56) * mm, "end": v(-177.1, 49.56) * mm});
            skLineSegment(sketch, "E76.0.2.21", {"start": v(-187.1, 52.56) * mm, "end": v(-187.1, 49.56) * mm});
            skLineSegment(sketch, "E76.0.2.22", {"start": v(-192.1, 52.56) * mm, "end": v(-192.1, 49.56) * mm});
            skLineSegment(sketch, "E76.0.2.23", {"start": v(-127.1, 52.56) * mm, "end": v(-127.1, 49.56) * mm});
            skLineSegment(sketch, "E76.0.2.24", {"start": v(-132.1, 52.56) * mm, "end": v(-132.1, 49.56) * mm});
            skLineSegment(sketch, "E76.0.2.25", {"start": v(-157.1, 52.56) * mm, "end": v(-157.1, 49.56) * mm});
            skLineSegment(sketch, "E76.0.2.26", {"start": v(-117.1, 52.56) * mm, "end": v(-117.1, 49.56) * mm});
            skLineSegment(sketch, "E76.0.2.27", {"start": v(-147.1, 52.56) * mm, "end": v(-147.1, 49.56) * mm});
            skLineSegment(sketch, "E76.0.2.28", {"start": v(-162.1, 52.56) * mm, "end": v(-162.1, 49.56) * mm});
            skLineSegment(sketch, "E76.0.2.29", {"start": v(-122.1, 52.56) * mm, "end": v(-122.1, 49.56) * mm});
            skLineSegment(sketch, "E76.0.2.30", {"start": v(-137.1, 52.56) * mm, "end": v(-137.1, 49.56) * mm});
            skLineSegment(sketch, "E76.0.2.31", {"start": v(-167.1, 52.56) * mm, "end": v(-167.1, 49.56) * mm});
            skLineSegment(sketch, "E76.0.2.32", {"start": v(-172.1, 52.56) * mm, "end": v(-172.1, 49.56) * mm});
            skLineSegment(sketch, "E76.0.3.0", {"start": v(-172.1, 150.56) * mm, "end": v(-167.1, 150.56) * mm});
            skLineSegment(sketch, "E76.0.3.1", {"start": v(-182.1, 153.56) * mm, "end": v(-177.1, 153.56) * mm});
            skLineSegment(sketch, "E76.0.3.2", {"start": v(-182.1, 150.56) * mm, "end": v(-177.1, 150.56) * mm});
            skLineSegment(sketch, "E76.0.3.3", {"start": v(-152.1, 153.56) * mm, "end": v(-147.1, 153.56) * mm});
            skLineSegment(sketch, "E76.0.3.4", {"start": v(-162.1, 153.56) * mm, "end": v(-157.1, 153.56) * mm});
            skLineSegment(sketch, "E76.0.3.5", {"start": v(-122.1, 153.56) * mm, "end": v(-117.1, 153.56) * mm});
            skLineSegment(sketch, "E76.0.3.6", {"start": v(-132.1, 150.56) * mm, "end": v(-127.1, 150.56) * mm});
            skLineSegment(sketch, "E76.0.3.7", {"start": v(-142.1, 150.56) * mm, "end": v(-137.1, 150.56) * mm});
            skLineSegment(sketch, "E76.0.3.8", {"start": v(-142.1, 153.56) * mm, "end": v(-137.1, 153.56) * mm});
            skLineSegment(sketch, "E76.0.3.9", {"start": v(-152.1, 150.56) * mm, "end": v(-147.1, 150.56) * mm});
            skLineSegment(sketch, "E76.0.3.10", {"start": v(-132.1, 153.56) * mm, "end": v(-127.1, 153.56) * mm});
            skLineSegment(sketch, "E76.0.3.11", {"start": v(-192.1, 150.56) * mm, "end": v(-182.1, 150.56) * mm, "construction": true});
            skLineSegment(sketch, "E76.0.3.12", {"start": v(-162.1, 150.56) * mm, "end": v(-157.1, 150.56) * mm});
            skLineSegment(sketch, "E76.0.3.13", {"start": v(-172.1, 153.56) * mm, "end": v(-167.1, 153.56) * mm});
            skLineSegment(sketch, "E76.0.3.14", {"start": v(-122.1, 150.56) * mm, "end": v(-117.1, 150.56) * mm});
            skLineSegment(sketch, "E76.0.3.15", {"start": v(-192.1, 153.56) * mm, "end": v(-187.1, 153.56) * mm});
            skLineSegment(sketch, "E76.0.3.16", {"start": v(-192.1, 150.56) * mm, "end": v(-187.1, 150.56) * mm});
            skLineSegment(sketch, "E76.0.3.17", {"start": v(-182.1, 153.56) * mm, "end": v(-182.1, 150.56) * mm});
            skLineSegment(sketch, "E76.0.3.18", {"start": v(-152.1, 153.56) * mm, "end": v(-152.1, 150.56) * mm});
            skLineSegment(sketch, "E76.0.3.19", {"start": v(-142.1, 153.56) * mm, "end": v(-142.1, 150.56) * mm});
            skLineSegment(sketch, "E76.0.3.20", {"start": v(-177.1, 153.56) * mm, "end": v(-177.1, 150.56) * mm});
            skLineSegment(sketch, "E76.0.3.21", {"start": v(-187.1, 153.56) * mm, "end": v(-187.1, 150.56) * mm});
            skLineSegment(sketch, "E76.0.3.22", {"start": v(-192.1, 153.56) * mm, "end": v(-192.1, 150.56) * mm});
            skLineSegment(sketch, "E76.0.3.23", {"start": v(-127.1, 153.56) * mm, "end": v(-127.1, 150.56) * mm});
            skLineSegment(sketch, "E76.0.3.24", {"start": v(-132.1, 153.56) * mm, "end": v(-132.1, 150.56) * mm});
            skLineSegment(sketch, "E76.0.3.25", {"start": v(-157.1, 153.56) * mm, "end": v(-157.1, 150.56) * mm});
            skLineSegment(sketch, "E76.0.3.26", {"start": v(-117.1, 153.56) * mm, "end": v(-117.1, 150.56) * mm});
            skLineSegment(sketch, "E76.0.3.27", {"start": v(-147.1, 153.56) * mm, "end": v(-147.1, 150.56) * mm});
            skLineSegment(sketch, "E76.0.3.28", {"start": v(-162.1, 153.56) * mm, "end": v(-162.1, 150.56) * mm});
            skLineSegment(sketch, "E76.0.3.29", {"start": v(-122.1, 153.56) * mm, "end": v(-122.1, 150.56) * mm});
            skLineSegment(sketch, "E76.0.3.30", {"start": v(-137.1, 153.56) * mm, "end": v(-137.1, 150.56) * mm});
            skLineSegment(sketch, "E76.0.3.31", {"start": v(-167.1, 153.56) * mm, "end": v(-167.1, 150.56) * mm});
            skLineSegment(sketch, "E76.0.3.32", {"start": v(-172.1, 153.56) * mm, "end": v(-172.1, 150.56) * mm});
            skLineSegment(sketch, "E76.direction1", {"start": v(-192.1, -152.44) * mm, "end": v(-167.1, -152.44) * mm, "construction": true});
            skLineSegment(sketch, "E76.direction2", {"start": v(-192.1, -152.44) * mm, "end": v(-192.1, -51.44) * mm, "construction": true});
            skSolve(sketch);
        }
        {
            var Q0;
            Q0 = qSketchRegion(id + "F15", true);
            extrude(context, id + "F16", {"entities" : qUnion([Q0]), "depth" : 3 * mm});
        }
    });
